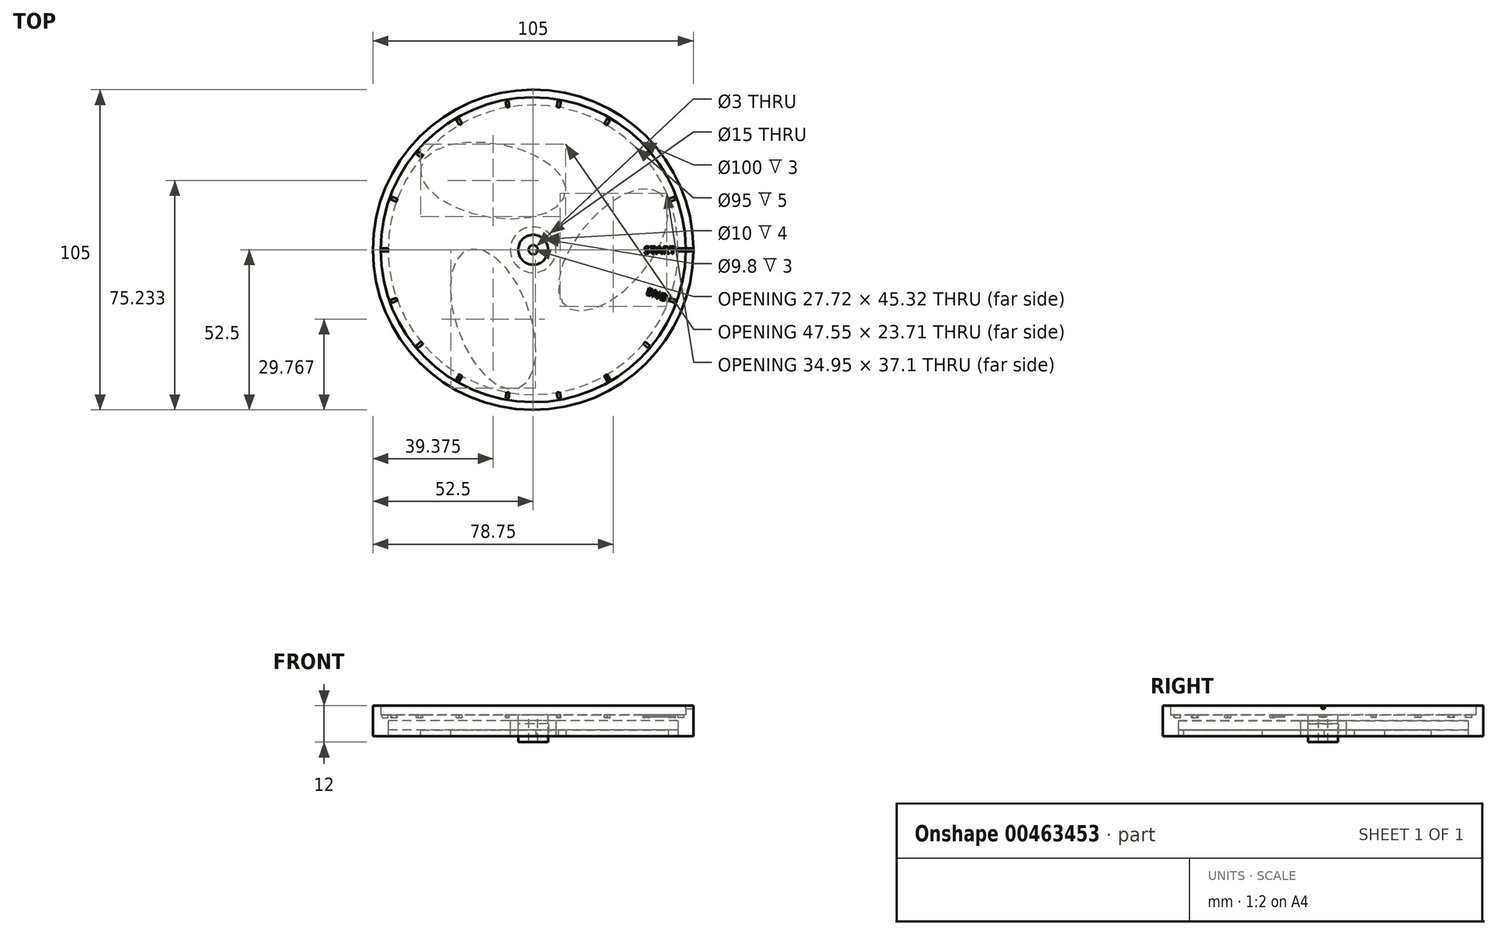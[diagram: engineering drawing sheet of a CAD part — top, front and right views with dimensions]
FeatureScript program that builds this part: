
annotation { "Feature Type Name" : "Feature", "Feature Type Description" : "" }
export const myFeature = defineFeature(function(context is Context, id is Id, definition is map)
    precondition{}
    {
        {
            var Q0;
            Q0=qCreatedBy(makeId("Top.planeOp"),FACE);
            var sketch = newSketch(context, id + "F0", { "sketchPlane" : qUnion([Q0])});
            skCircle(sketch, "E0", {"center": v(0, 0) * mm, "radius": 50 * mm});
            skCircle(sketch, "E1", {"center": v(0, 0) * mm, "radius": 52.5 * mm});
            skPoint(sketch, "E2.middle", {"position": v(52.5, 0) * mm});
            skCircle(sketch, "E3", {"center": v(0, 0) * mm, "radius": 5 * mm});
            skCircle(sketch, "E4", {"center": v(0, 0) * mm, "radius": 7.5 * mm});
            skCircle(sketch, "E5", {"center": v(0, 0) * mm, "radius": 47.5 * mm});
            skEllipse(sketch, "E6", {"center": v(26.25, 0) * mm, "majorRadius": 24.13 * mm, "minorRadius": 12.04 * mm, "majorAxis": v(0.64, 0.77)});
            skFitSpline(sketch, "E7.0", {"points": [v(47.3, 21.48) * mm, v(45.63, 23.18) * mm, v(43.65, 24.52) * mm, v(41.5, 25.44) * mm, v(39.28, 25.95) * mm, v(37.04, 26.11) * mm, v(34.8, 25.97) * mm, v(31.85, 25.42) * mm, v(28.25, 24.17) * mm, v(24.72, 22.3) * mm, v(21.93, 20.46) * mm, v(19.22, 18.43) * mm, v(16.62, 16.12) * mm, v(14.16, 13.59) * mm, v(12.4, 11.58) * mm, v(10.73, 9.49) * mm, v(8.67, 6.62) * mm, v(6.87, 3.65) * mm, v(5.35, 0.62) * mm, v(4.03, -2.45) * mm, v(2.81, -6.26) * mm, v(2.23, -10.02) * mm, v(2.21, -13.03) * mm, v(2.47, -15.25) * mm, v(3.02, -17.43) * mm, v(3.92, -19.53) * mm, v(5.2, -21.48) * mm, v(6.87, -23.18) * mm, v(8.85, -24.52) * mm, v(11, -25.44) * mm, v(13.22, -25.95) * mm, v(15.46, -26.11) * mm, v(17.7, -25.97) * mm, v(20.65, -25.42) * mm, v(24.25, -24.17) * mm, v(27.78, -22.3) * mm, v(30.57, -20.46) * mm, v(33.28, -18.43) * mm, v(35.88, -16.12) * mm, v(38.34, -13.59) * mm, v(40.1, -11.58) * mm, v(41.77, -9.49) * mm, v(43.83, -6.62) * mm, v(45.63, -3.65) * mm, v(47.15, -0.62) * mm, v(48.47, 2.45) * mm, v(49.69, 6.26) * mm, v(50.27, 10.02) * mm, v(50.29, 13.03) * mm, v(50.03, 15.25) * mm, v(49.48, 17.43) * mm, v(48.58, 19.53) * mm, v(47.3, 21.48) * mm, v(45.63, 23.18) * mm, v(43.65, 24.52) * mm, v(47.3, 21.48) * mm]});
            skEllipse(sketch, "E8.1.0", {"center": v(-13.12, 22.73) * mm, "majorRadius": 24.13 * mm, "minorRadius": 12.04 * mm, "majorAxis": v(-0.99, 0.17)});
            skEllipse(sketch, "E8.2.0", {"center": v(-13.13, -22.73) * mm, "majorRadius": 24.13 * mm, "minorRadius": 12.04 * mm, "majorAxis": v(0.34, -0.94)});
            skFitSpline(sketch, "E9.0", {"points": [v(-42.25, 30.22) * mm, v(-42.89, 27.92) * mm, v(-43.06, 25.54) * mm, v(-42.78, 23.23) * mm, v(-42.11, 21.04) * mm, v(-41.13, 19.02) * mm, v(-39.9, 17.16) * mm, v(-37.94, 14.87) * mm, v(-35.06, 12.37) * mm, v(-31.67, 10.25) * mm, v(-28.69, 8.76) * mm, v(-25.57, 7.43) * mm, v(-22.27, 6.33) * mm, v(-18.85, 5.47) * mm, v(-16.23, 4.94) * mm, v(-13.58, 4.55) * mm, v(-10.07, 4.2) * mm, v(-6.6, 4.12) * mm, v(-3.2, 4.32) * mm, v(0.1, 4.71) * mm, v(4.01, 5.56) * mm, v(7.57, 6.94) * mm, v(10.18, 8.43) * mm, v(11.97, 9.76) * mm, v(13.58, 11.33) * mm, v(14.95, 13.16) * mm, v(16, 15.25) * mm, v(16.64, 17.54) * mm, v(16.81, 19.92) * mm, v(16.53, 22.24) * mm, v(15.86, 24.43) * mm, v(14.88, 26.45) * mm, v(13.64, 28.3) * mm, v(11.7, 30.6) * mm, v(8.8, 33.1) * mm, v(5.42, 35.21) * mm, v(2.44, 36.7) * mm, v(-0.68, 38.04) * mm, v(-3.98, 39.14) * mm, v(-7.4, 40) * mm, v(-10.02, 40.52) * mm, v(-12.67, 40.92) * mm, v(-16.18, 41.26) * mm, v(-19.65, 41.34) * mm, v(-23.04, 41.15) * mm, v(-26.36, 40.75) * mm, v(-30.26, 39.9) * mm, v(-33.82, 38.53) * mm, v(-36.43, 37.04) * mm, v(-38.22, 35.7) * mm, v(-39.83, 34.13) * mm, v(-41.2, 32.3) * mm, v(-42.25, 30.22) * mm, v(-42.89, 27.92) * mm, v(-43.06, 25.54) * mm, v(-42.25, 30.22) * mm]});
            skFitSpline(sketch, "E10.0", {"points": [v(-5.04, -51.7) * mm, v(-2.74, -51.1) * mm, v(-0.6, -50.06) * mm, v(1.28, -48.66) * mm, v(2.84, -47) * mm, v(4.1, -45.13) * mm, v(5.09, -43.13) * mm, v(6.1, -40.3) * mm, v(6.81, -36.55) * mm, v(6.96, -32.56) * mm, v(6.75, -29.22) * mm, v(6.35, -25.85) * mm, v(5.65, -22.45) * mm, v(4.69, -19.06) * mm, v(3.83, -16.52) * mm, v(2.85, -14.04) * mm, v(1.4, -10.82) * mm, v(-0.27, -7.77) * mm, v(-2.14, -4.94) * mm, v(-4.14, -2.26) * mm, v(-6.82, 0.7) * mm, v(-9.8, 3.08) * mm, v(-12.39, 4.6) * mm, v(-14.44, 5.49) * mm, v(-16.6, 6.1) * mm, v(-18.87, 6.37) * mm, v(-21.2, 6.23) * mm, v(-23.51, 5.64) * mm, v(-25.66, 4.6) * mm, v(-27.53, 3.2) * mm, v(-29.09, 1.53) * mm, v(-30.35, -0.33) * mm, v(-31.34, -2.34) * mm, v(-32.34, -5.17) * mm, v(-33.06, -8.92) * mm, v(-33.2, -12.9) * mm, v(-33, -16.24) * mm, v(-32.6, -19.61) * mm, v(-31.9, -23.02) * mm, v(-30.94, -26.4) * mm, v(-30.08, -28.94) * mm, v(-29.1, -31.43) * mm, v(-27.65, -34.64) * mm, v(-25.98, -37.7) * mm, v(-24.11, -40.53) * mm, v(-22.11, -43.2) * mm, v(-19.43, -46.16) * mm, v(-16.46, -48.55) * mm, v(-13.86, -50.06) * mm, v(-11.8, -50.96) * mm, v(-9.65, -51.56) * mm, v(-7.38, -51.83) * mm, v(-5.04, -51.7) * mm, v(-2.74, -51.1) * mm, v(-0.6, -50.06) * mm, v(-5.04, -51.7) * mm]});
            skSolve(sketch);
        }
        {
            var Q0;
            {var subQ0=sQuery(id+"F0.wireOp",EDGE,"E9.0");var subQ1=sQuery(id+"F0.wireOp",EDGE,"E0");var subQ2=makeQuery(id+"F0.imprint","INTERSECT",VERTEX,{"disambiguationData":[OD(1.0)],"derivedFrom":[subQ1,subQ0]});Q0=makeQuery(id+"F0.imprint","IMPRINT",FACE,{"disambiguationData":[TD([[makeQuery(id+"F0.imprint","IMPRINT",EDGE,{"disambiguationData":[TD([[subQ2,-1.0]])],"derivedFrom":subQ1}),1.0]])]});}
            var Q1;
            {var subQ0=sQuery(id+"F0.wireOp",EDGE,"E10.0");var subQ1=sQuery(id+"F0.wireOp",EDGE,"E0");var subQ2=makeQuery(id+"F0.imprint","INTERSECT",VERTEX,{"disambiguationData":[OD(0.0)],"derivedFrom":[subQ1,subQ0]});Q1=makeQuery(id+"F0.imprint","IMPRINT",FACE,{"disambiguationData":[TD([[makeQuery(id+"F0.imprint","IMPRINT",EDGE,{"disambiguationData":[TD([[subQ2,-1.0]])],"derivedFrom":subQ1}),1.0]])]});}
            var Q2;
            {var subQ0=sQuery(id+"F0.wireOp",EDGE,"E7.0");var subQ1=sQuery(id+"F0.wireOp",EDGE,"E0");var subQ2=makeQuery(id+"F0.imprint","INTERSECT",VERTEX,{"disambiguationData":[OD(1.0)],"derivedFrom":[subQ1,subQ0]});Q2=makeQuery(id+"F0.imprint","IMPRINT",FACE,{"disambiguationData":[TD([[makeQuery(id+"F0.imprint","IMPRINT",EDGE,{"disambiguationData":[TD([[subQ2,1.0]])],"derivedFrom":subQ1}),1.0]])]});}
            var Q3;
            {var subQ0=sQuery(id+"F0.wireOp",EDGE,"E7.0");var subQ1=sQuery(id+"F0.wireOp",EDGE,"E0");var subQ2=makeQuery(id+"F0.imprint","INTERSECT",VERTEX,{"disambiguationData":[OD(0.0)],"derivedFrom":[subQ1,subQ0]});Q3=makeQuery(id+"F0.imprint","IMPRINT",FACE,{"disambiguationData":[TD([[makeQuery(id+"F0.imprint","IMPRINT",EDGE,{"disambiguationData":[TD([[subQ2,1.0]])],"derivedFrom":subQ1}),1.0]])]});}
            var Q4;
            {var subQ0=sQuery(id+"F0.wireOp",EDGE,"E7.0");var subQ1=sQuery(id+"F0.wireOp",EDGE,"E0");var subQ2=makeQuery(id+"F0.imprint","INTERSECT",VERTEX,{"disambiguationData":[OD(0.0)],"derivedFrom":[subQ1,subQ0]});Q4=makeQuery(id+"F0.imprint","IMPRINT",FACE,{"disambiguationData":[TD([[makeQuery(id+"F0.imprint","IMPRINT",EDGE,{"disambiguationData":[TD([[subQ2,-1.0]])],"derivedFrom":subQ1}),1.0]])]});}
            var Q5;
            {var subQ0=sQuery(id+"F0.wireOp",EDGE,"E9.0");var subQ1=sQuery(id+"F0.wireOp",EDGE,"E0");var subQ2=makeQuery(id+"F0.imprint","INTERSECT",VERTEX,{"disambiguationData":[OD(0.0)],"derivedFrom":[subQ1,subQ0]});Q5=makeQuery(id+"F0.imprint","IMPRINT",FACE,{"disambiguationData":[TD([[makeQuery(id+"F0.imprint","IMPRINT",EDGE,{"disambiguationData":[TD([[subQ2,-1.0]])],"derivedFrom":subQ1}),1.0]])]});}
            var Q6;
            Q6=makeQuery(id+"F0.imprint","IMPRINT",FACE,{"disambiguationData":[TD([[makeQuery(id+"F0.imprint","IMPRINT",EDGE,{"derivedFrom":sQuery(id+"F0.wireOp",EDGE,"5SP7GSyY-g8OX-zm8A-jqP5-KDN9Loz0VI4X")}),-1.0]])]});
            var Q7;
            {var subQ0=sQuery(id+"F0.wireOp",EDGE,"E9.0");var subQ1=sQuery(id+"F0.wireOp",EDGE,"E3");var subQ2=makeQuery(id+"F0.imprint","INTERSECT",VERTEX,{"disambiguationData":[OD(0.0)],"derivedFrom":[subQ1,subQ0]});Q7=makeQuery(id+"F0.imprint","IMPRINT",FACE,{"disambiguationData":[TD([[makeQuery(id+"F0.imprint","IMPRINT",EDGE,{"disambiguationData":[TD([[subQ2,-1.0]])],"derivedFrom":subQ1}),-1.0]])]});}
            var Q8;
            {var subQ0=sQuery(id+"F0.wireOp",EDGE,"E9.0");var subQ1=sQuery(id+"F0.wireOp",EDGE,"E3");var subQ2=makeQuery(id+"F0.imprint","INTERSECT",VERTEX,{"disambiguationData":[OD(0.0)],"derivedFrom":[subQ1,subQ0]});Q8=makeQuery(id+"F0.imprint","IMPRINT",FACE,{"disambiguationData":[TD([[makeQuery(id+"F0.imprint","IMPRINT",EDGE,{"disambiguationData":[TD([[subQ2,1.0]])],"derivedFrom":subQ1}),-1.0]])]});}
            var Q9;
            {var subQ0=sQuery(id+"F0.wireOp",EDGE,"E9.0");var subQ1=sQuery(id+"F0.wireOp",EDGE,"E3");var subQ2=makeQuery(id+"F0.imprint","INTERSECT",VERTEX,{"disambiguationData":[OD(1.0)],"derivedFrom":[subQ1,subQ0]});Q9=makeQuery(id+"F0.imprint","IMPRINT",FACE,{"disambiguationData":[TD([[makeQuery(id+"F0.imprint","IMPRINT",EDGE,{"disambiguationData":[TD([[subQ2,1.0]])],"derivedFrom":subQ1}),-1.0]])]});}
            var Q10;
            {var subQ0=sQuery(id+"F0.wireOp",EDGE,"E7.0");var subQ1=sQuery(id+"F0.wireOp",EDGE,"E3");var subQ2=makeQuery(id+"F0.imprint","INTERSECT",VERTEX,{"disambiguationData":[OD(0.0)],"derivedFrom":[subQ1,subQ0]});Q10=makeQuery(id+"F0.imprint","IMPRINT",FACE,{"disambiguationData":[TD([[makeQuery(id+"F0.imprint","IMPRINT",EDGE,{"disambiguationData":[TD([[subQ2,-1.0]])],"derivedFrom":subQ1}),-1.0]])]});}
            var Q11;
            {var subQ0=sQuery(id+"F0.wireOp",EDGE,"E10.0");var subQ1=sQuery(id+"F0.wireOp",EDGE,"E3");var subQ2=makeQuery(id+"F0.imprint","INTERSECT",VERTEX,{"disambiguationData":[OD(0.0)],"derivedFrom":[subQ1,subQ0]});Q11=makeQuery(id+"F0.imprint","IMPRINT",FACE,{"disambiguationData":[TD([[makeQuery(id+"F0.imprint","IMPRINT",EDGE,{"disambiguationData":[TD([[subQ2,-1.0]])],"derivedFrom":subQ1}),-1.0]])]});}
            var Q12;
            {var subQ0=sQuery(id+"F0.wireOp",EDGE,"E10.0");var subQ1=sQuery(id+"F0.wireOp",EDGE,"E3");var subQ2=makeQuery(id+"F0.imprint","INTERSECT",VERTEX,{"disambiguationData":[OD(1.0)],"derivedFrom":[subQ1,subQ0]});Q12=makeQuery(id+"F0.imprint","IMPRINT",FACE,{"disambiguationData":[TD([[makeQuery(id+"F0.imprint","IMPRINT",EDGE,{"disambiguationData":[TD([[subQ2,-1.0]])],"derivedFrom":subQ1}),-1.0]])]});}
            extrude(context, id + "F1", {"entities" : qUnion([Q0, Q1, Q2, Q3, Q4, Q5, Q6, Q7, Q8, Q9, Q10, Q11, Q12]), "depth" : 7 * mm});
        }
        {
            var Q0;
            Q0=makeQuery(id+"F0.imprint","IMPRINT",FACE,{"disambiguationData":[TD([[makeQuery(id+"F0.imprint","IMPRINT",EDGE,{"derivedFrom":sQuery(id+"F0.wireOp",EDGE,"E1")}),1.0]])]});
            var Q1;
            {var subQ0=sQuery(id+"F0.wireOp",EDGE,"E7.0");var subQ1=sQuery(id+"F0.wireOp",EDGE,"E0");var subQ2=makeQuery(id+"F0.imprint","INTERSECT",VERTEX,{"disambiguationData":[OD(0.0)],"derivedFrom":[subQ1,subQ0]});Q1=makeQuery(id+"F0.imprint","IMPRINT",FACE,{"disambiguationData":[TD([[makeQuery(id+"F0.imprint","IMPRINT",EDGE,{"disambiguationData":[TD([[subQ2,1.0]])],"derivedFrom":subQ1}),-1.0]])]});}
            var Q2;
            {var subQ0=sQuery(id+"F0.wireOp",EDGE,"E10.0");var subQ1=sQuery(id+"F0.wireOp",EDGE,"E0");var subQ2=makeQuery(id+"F0.imprint","INTERSECT",VERTEX,{"disambiguationData":[OD(0.0)],"derivedFrom":[subQ1,subQ0]});Q2=makeQuery(id+"F0.imprint","IMPRINT",FACE,{"disambiguationData":[TD([[makeQuery(id+"F0.imprint","IMPRINT",EDGE,{"disambiguationData":[TD([[subQ2,-1.0]])],"derivedFrom":subQ1}),-1.0]])]});}
            var Q3;
            {var subQ0=sQuery(id+"F0.wireOp",EDGE,"E9.0");var subQ1=sQuery(id+"F0.wireOp",EDGE,"E0");var subQ2=makeQuery(id+"F0.imprint","INTERSECT",VERTEX,{"disambiguationData":[OD(0.0)],"derivedFrom":[subQ1,subQ0]});Q3=makeQuery(id+"F0.imprint","IMPRINT",FACE,{"disambiguationData":[TD([[makeQuery(id+"F0.imprint","IMPRINT",EDGE,{"disambiguationData":[TD([[subQ2,-1.0]])],"derivedFrom":subQ1}),-1.0]])]});}
            extrude(context, id + "F2", {"entities" : qUnion([Q0, Q1, Q2, Q3]), "operationType" : NewBodyOperationType.ADD, "depth" : 10 * mm});
        }
        {
            var Q0;
            Q0=makeQuery(id+"F0.imprint","IMPRINT",FACE,{"disambiguationData":[TD([[makeQuery(id+"F0.imprint","IMPRINT",EDGE,{"derivedFrom":sQuery(id+"F0.wireOp",EDGE,"E8.1.0")}),-1.0]])]});
            var Q1;
            {var subQ0=sQuery(id+"F0.wireOp",EDGE,"E10.0");var subQ1=sQuery(id+"F0.wireOp",EDGE,"E9.0");var subQ2=makeQuery(id+"F0.imprint","INTERSECT",VERTEX,{"disambiguationData":[OD(0.0)],"derivedFrom":[subQ1,subQ0]});Q1=makeQuery(id+"F0.imprint","IMPRINT",FACE,{"disambiguationData":[TD([[makeQuery(id+"F0.imprint","IMPRINT",EDGE,{"disambiguationData":[TD([[subQ2,-1.0]])],"derivedFrom":subQ1}),1.0]])]});}
            var Q2;
            Q2=makeQuery(id+"F0.imprint","IMPRINT",FACE,{"disambiguationData":[TD([[makeQuery(id+"F0.imprint","IMPRINT",EDGE,{"derivedFrom":sQuery(id+"F0.wireOp",EDGE,"E8.2.0")}),-1.0]])]});
            var Q3;
            {var subQ0=sQuery(id+"F0.wireOp",EDGE,"E9.0");var subQ1=sQuery(id+"F0.wireOp",EDGE,"E4");var subQ2=makeQuery(id+"F0.imprint","INTERSECT",VERTEX,{"disambiguationData":[OD(1.0)],"derivedFrom":[subQ1,subQ0]});Q3=makeQuery(id+"F0.imprint","IMPRINT",FACE,{"disambiguationData":[TD([[makeQuery(id+"F0.imprint","IMPRINT",EDGE,{"disambiguationData":[TD([[subQ2,-1.0]])],"derivedFrom":subQ1}),-1.0]])]});}
            var Q4;
            {var subQ0=sQuery(id+"F0.wireOp",EDGE,"E10.0");var subQ1=sQuery(id+"F0.wireOp",EDGE,"E4");var subQ2=makeQuery(id+"F0.imprint","INTERSECT",VERTEX,{"disambiguationData":[OD(1.0)],"derivedFrom":[subQ1,subQ0]});Q4=makeQuery(id+"F0.imprint","IMPRINT",FACE,{"disambiguationData":[TD([[makeQuery(id+"F0.imprint","IMPRINT",EDGE,{"disambiguationData":[TD([[subQ2,-1.0]])],"derivedFrom":subQ1}),-1.0]])]});}
            var Q5;
            {var subQ0=sQuery(id+"F0.wireOp",EDGE,"E10.0");var subQ1=sQuery(id+"F0.wireOp",EDGE,"E7.0");var subQ2=makeQuery(id+"F0.imprint","INTERSECT",VERTEX,{"disambiguationData":[OD(0.0)],"derivedFrom":[subQ1,subQ0]});Q5=makeQuery(id+"F0.imprint","IMPRINT",FACE,{"disambiguationData":[TD([[makeQuery(id+"F0.imprint","IMPRINT",EDGE,{"disambiguationData":[TD([[subQ2,-1.0]])],"derivedFrom":subQ1}),1.0]])]});}
            var Q6;
            Q6=makeQuery(id+"F0.imprint","IMPRINT",FACE,{"disambiguationData":[TD([[makeQuery(id+"F0.imprint","IMPRINT",EDGE,{"derivedFrom":sQuery(id+"F0.wireOp",EDGE,"E6")}),-1.0]])]});
            var Q7;
            {var subQ0=sQuery(id+"F0.wireOp",EDGE,"E9.0");var subQ1=sQuery(id+"F0.wireOp",EDGE,"E4");var subQ2=makeQuery(id+"F0.imprint","INTERSECT",VERTEX,{"disambiguationData":[OD(0.0)],"derivedFrom":[subQ1,subQ0]});Q7=makeQuery(id+"F0.imprint","IMPRINT",FACE,{"disambiguationData":[TD([[makeQuery(id+"F0.imprint","IMPRINT",EDGE,{"disambiguationData":[TD([[subQ2,1.0]])],"derivedFrom":subQ1}),-1.0]])]});}
            var Q8;
            {var subQ0=sQuery(id+"F0.wireOp",EDGE,"E9.0");var subQ1=sQuery(id+"F0.wireOp",EDGE,"E7.0");var subQ2=makeQuery(id+"F0.imprint","INTERSECT",VERTEX,{"disambiguationData":[OD(0.0)],"derivedFrom":[subQ1,subQ0]});Q8=makeQuery(id+"F0.imprint","IMPRINT",FACE,{"disambiguationData":[TD([[makeQuery(id+"F0.imprint","IMPRINT",EDGE,{"disambiguationData":[TD([[subQ2,-1.0]])],"derivedFrom":subQ1}),1.0]])]});}
            extrude(context, id + "F3", {"entities" : qUnion([Q0, Q1, Q2, Q3, Q4, Q5, Q6, Q7, Q8]), "depth" : 2 * mm});
        }
        {
            var Q0;
            Q0=makeQuery(id+"F1.opExtrude","CAP_FACE",FACE,{"disambiguationData":[OSD([sQuery(id+"F0.wireOp",EDGE,"E3"),sQuery(id+"F0.wireOp",EDGE,"E4")])],"isStart":false});
            var sketch = newSketch(context, id + "F4", { "sketchPlane" : qUnion([Q0])});
            skCircle(sketch, "E11", {"center": v(0, 0) * mm, "radius": 4.9 * mm});
            skCircle(sketch, "E12", {"center": v(0, 0) * mm, "radius": 49.5 * mm});
            skCircle(sketch, "E13.0", {"center": v(0, 0) * mm, "radius": 47.5 * mm});
            skCircle(sketch, "E14", {"center": v(0, 0) * mm, "radius": 7.5 * mm});
            skSolve(sketch);
        }
        {
            var Q0;
            Q0=makeQuery(id+"F4.imprint","IMPRINT",FACE,{"disambiguationData":[TD([[makeQuery(id+"F4.imprint","IMPRINT",EDGE,{"derivedFrom":sQuery(id+"F4.wireOp",EDGE,"E11")}),1.0]])]});
            extrude(context, id + "F5", {"entities" : qUnion([Q0]), "oppositeDirection" : true, "depth" : 9 * mm});
        }
        {
            var Q0;
            Q0=makeQuery(id+"F4.imprint","IMPRINT",FACE,{"disambiguationData":[TD([[makeQuery(id+"F4.imprint","IMPRINT",EDGE,{"derivedFrom":sQuery(id+"F4.wireOp",EDGE,"E14")}),1.0]])]});
            var Q1;
            Q1=makeQuery(id+"F4.imprint","IMPRINT",FACE,{"disambiguationData":[TD([[makeQuery(id+"F4.imprint","IMPRINT",EDGE,{"derivedFrom":sQuery(id+"F4.wireOp",EDGE,"E11")}),-1.0]])]});
            extrude(context, id + "F6", {"entities" : qUnion([Q0, Q1]), "oppositeDirection" : true, "depth" : 3 * mm});
        }
        {
            var Q0;
            Q0=makeQuery(id+"F4.imprint","IMPRINT",FACE,{"disambiguationData":[TD([[makeQuery(id+"F4.imprint","IMPRINT",EDGE,{"derivedFrom":sQuery(id+"F4.wireOp",EDGE,"E13.0")}),1.0]])]});
            extrude(context, id + "F7", {"entities" : qUnion([Q0]), "operationType" : NewBodyOperationType.ADD, "oppositeDirection" : true, "depth" : 2 * mm});
        }
        {
            var Q0;
            Q0=makeQuery(id+"F4.imprint","IMPRINT",FACE,{"disambiguationData":[TD([[makeQuery(id+"F4.imprint","IMPRINT",EDGE,{"derivedFrom":sQuery(id+"F4.wireOp",EDGE,"E12")}),1.0]])]});
            extrude(context, id + "F8", {"entities" : qUnion([Q0]), "operationType" : NewBodyOperationType.ADD, "oppositeDirection" : true, "depth" : 3 * mm});
        }
        {
            var Q0;
            Q0=makeQuery(id+"F2.opExtrude","CAP_FACE",FACE,{"disambiguationData":[OSD([sQuery(id+"F0.wireOp",EDGE,"E0"),sQuery(id+"F0.wireOp",EDGE,"E1")])],"isStart":false});
            var sketch = newSketch(context, id + "F9", { "sketchPlane" : qUnion([Q0])});
            skLineSegment(sketch, "E15", {"start": v(0, 0) * mm, "end": v(52.5, 0) * mm, "construction": true});
            skLineSegment(sketch, "E16.bottom", {"start": v(49.7, -0.5) * mm, "end": v(55.3, -0.5) * mm});
            skLineSegment(sketch, "E16.top", {"start": v(49.7, 0.5) * mm, "end": v(55.3, 0.5) * mm});
            skLineSegment(sketch, "E16.left", {"start": v(49.7, -0.5) * mm, "end": v(49.7, 0.5) * mm});
            skLineSegment(sketch, "E16.right", {"start": v(55.3, -0.5) * mm, "end": v(55.3, 0.5) * mm});
            skPoint(sketch, "E16.middle", {"position": v(52.5, 0) * mm});
            skSolve(sketch);
        }
        {
            var Q0;
            {var subQ0=sQuery(id+"F9.wireOp",EDGE,"E16.bottom");var subQ1=makeQuery(id+"F2.opExtrude","CAP_EDGE",EDGE,{"disambiguationData":[OSD([sQuery(id+"F0.wireOp",EDGE,"E1")])],"isStart":false});var subQ2=makeQuery(id+"F9.imprint","INTERSECT",VERTEX,{"derivedFrom":[subQ1,subQ0]});Q0=makeQuery(id+"F9.imprint","IMPRINT",FACE,{"disambiguationData":[TD([[makeQuery(id+"F9.imprint","IMPRINT",EDGE,{"disambiguationData":[TD([[subQ2,1.0]])],"derivedFrom":subQ0}),1.0]])]});}
            extrude(context, id + "F10", {"entities" : qUnion([Q0]), "operationType" : NewBodyOperationType.REMOVE, "oppositeDirection" : true, "depth" : 1 * mm});
        }
        {
            var Q0;
            Q0=makeQuery(id+"F4.imprint","IMPRINT",FACE,{"disambiguationData":[TD([[makeQuery(id+"F4.imprint","IMPRINT",EDGE,{"derivedFrom":sQuery(id+"F4.wireOp",EDGE,"E12")}),1.0]])]});
            var sketch = newSketch(context, id + "F11", { "sketchPlane" : qUnion([Q0])});
            skCircle(sketch, "E17.0", {"center": v(0, 0) * mm, "radius": 47.5 * mm});
            skCircle(sketch, "E18.0", {"center": v(0, 0) * mm, "radius": 49.5 * mm});
            skLineSegment(sketch, "E19", {"start": v(0, 0) * mm, "end": v(49.5, 0) * mm, "construction": true});
            skLineSegment(sketch, "E20.bottom", {"start": v(52.3, -0.5) * mm, "end": v(46.7, -0.5) * mm});
            skLineSegment(sketch, "E20.top", {"start": v(52.3, 0.5) * mm, "end": v(46.7, 0.5) * mm});
            skLineSegment(sketch, "E20.left", {"start": v(52.3, -0.5) * mm, "end": v(52.3, 0.5) * mm});
            skLineSegment(sketch, "E20.right", {"start": v(46.7, -0.5) * mm, "end": v(46.7, 0.5) * mm});
            skPoint(sketch, "E20.middle", {"position": v(49.5, 0) * mm});
            skLineSegment(sketch, "E21.1.0", {"start": v(49.31, -17.42) * mm, "end": v(44.06, -15.5) * mm});
            skLineSegment(sketch, "E21.1.1", {"start": v(48.97, -18.36) * mm, "end": v(43.72, -16.44) * mm});
            skLineSegment(sketch, "E21.1.2", {"start": v(43.72, -16.44) * mm, "end": v(44.06, -15.5) * mm});
            skLineSegment(sketch, "E21.1.3", {"start": v(48.97, -18.36) * mm, "end": v(49.31, -17.42) * mm});
            skLineSegment(sketch, "E21.2.0", {"start": v(40.38, -33.23) * mm, "end": v(36.1, -29.64) * mm});
            skLineSegment(sketch, "E21.2.1", {"start": v(39.74, -34) * mm, "end": v(35.46, -30.4) * mm});
            skLineSegment(sketch, "E21.2.2", {"start": v(35.46, -30.4) * mm, "end": v(36.1, -29.64) * mm});
            skLineSegment(sketch, "E21.2.3", {"start": v(39.74, -34) * mm, "end": v(40.38, -33.23) * mm});
            skLineSegment(sketch, "E21.3.0", {"start": v(26.58, -45.04) * mm, "end": v(23.79, -40.2) * mm});
            skLineSegment(sketch, "E21.3.1", {"start": v(25.71, -45.54) * mm, "end": v(22.92, -40.7) * mm});
            skLineSegment(sketch, "E21.3.2", {"start": v(22.92, -40.7) * mm, "end": v(23.79, -40.2) * mm});
            skLineSegment(sketch, "E21.3.3", {"start": v(25.71, -45.54) * mm, "end": v(26.58, -45.04) * mm});
            skLineSegment(sketch, "E21.4.0", {"start": v(9.57, -51.41) * mm, "end": v(8.6, -45.91) * mm});
            skLineSegment(sketch, "E21.4.1", {"start": v(8.59, -51.59) * mm, "end": v(7.62, -46.08) * mm});
            skLineSegment(sketch, "E21.4.2", {"start": v(7.62, -46.08) * mm, "end": v(8.6, -45.91) * mm});
            skLineSegment(sketch, "E21.4.3", {"start": v(8.59, -51.59) * mm, "end": v(9.57, -51.41) * mm});
            skLineSegment(sketch, "E21.5.0", {"start": v(-8.59, -51.59) * mm, "end": v(-7.62, -46.08) * mm});
            skLineSegment(sketch, "E21.5.1", {"start": v(-9.57, -51.41) * mm, "end": v(-8.6, -45.91) * mm});
            skLineSegment(sketch, "E21.5.2", {"start": v(-8.6, -45.91) * mm, "end": v(-7.62, -46.08) * mm});
            skLineSegment(sketch, "E21.5.3", {"start": v(-9.57, -51.41) * mm, "end": v(-8.59, -51.59) * mm});
            skLineSegment(sketch, "E21.6.0", {"start": v(-25.71, -45.54) * mm, "end": v(-22.92, -40.7) * mm});
            skLineSegment(sketch, "E21.6.1", {"start": v(-26.58, -45.04) * mm, "end": v(-23.79, -40.2) * mm});
            skLineSegment(sketch, "E21.6.2", {"start": v(-23.79, -40.2) * mm, "end": v(-22.92, -40.7) * mm});
            skLineSegment(sketch, "E21.6.3", {"start": v(-26.58, -45.04) * mm, "end": v(-25.71, -45.54) * mm});
            skLineSegment(sketch, "E21.7.0", {"start": v(-39.74, -34) * mm, "end": v(-35.46, -30.4) * mm});
            skLineSegment(sketch, "E21.7.1", {"start": v(-40.38, -33.23) * mm, "end": v(-36.1, -29.64) * mm});
            skLineSegment(sketch, "E21.7.2", {"start": v(-36.1, -29.64) * mm, "end": v(-35.46, -30.4) * mm});
            skLineSegment(sketch, "E21.7.3", {"start": v(-40.38, -33.23) * mm, "end": v(-39.74, -34) * mm});
            skLineSegment(sketch, "E21.8.0", {"start": v(-48.97, -18.36) * mm, "end": v(-43.72, -16.44) * mm});
            skLineSegment(sketch, "E21.8.1", {"start": v(-49.31, -17.42) * mm, "end": v(-44.06, -15.5) * mm});
            skLineSegment(sketch, "E21.8.2", {"start": v(-44.06, -15.5) * mm, "end": v(-43.72, -16.44) * mm});
            skLineSegment(sketch, "E21.8.3", {"start": v(-49.31, -17.42) * mm, "end": v(-48.97, -18.36) * mm});
            skLineSegment(sketch, "E21.9.0", {"start": v(-52.3, -0.5) * mm, "end": v(-46.7, -0.5) * mm});
            skLineSegment(sketch, "E21.9.1", {"start": v(-52.3, 0.5) * mm, "end": v(-46.7, 0.5) * mm});
            skLineSegment(sketch, "E21.9.2", {"start": v(-46.7, 0.5) * mm, "end": v(-46.7, -0.5) * mm});
            skLineSegment(sketch, "E21.9.3", {"start": v(-52.3, 0.5) * mm, "end": v(-52.3, -0.5) * mm});
            skLineSegment(sketch, "E21.10.0", {"start": v(-49.31, 17.42) * mm, "end": v(-44.06, 15.5) * mm});
            skLineSegment(sketch, "E21.10.1", {"start": v(-48.97, 18.36) * mm, "end": v(-43.72, 16.44) * mm});
            skLineSegment(sketch, "E21.10.2", {"start": v(-43.72, 16.44) * mm, "end": v(-44.06, 15.5) * mm});
            skLineSegment(sketch, "E21.10.3", {"start": v(-48.97, 18.36) * mm, "end": v(-49.31, 17.42) * mm});
            skLineSegment(sketch, "E21.11.0", {"start": v(-40.38, 33.23) * mm, "end": v(-36.1, 29.64) * mm});
            skLineSegment(sketch, "E21.11.1", {"start": v(-39.74, 34) * mm, "end": v(-35.46, 30.4) * mm});
            skLineSegment(sketch, "E21.11.2", {"start": v(-35.46, 30.4) * mm, "end": v(-36.1, 29.64) * mm});
            skLineSegment(sketch, "E21.11.3", {"start": v(-39.74, 34) * mm, "end": v(-40.38, 33.23) * mm});
            skLineSegment(sketch, "E21.12.0", {"start": v(-26.58, 45.04) * mm, "end": v(-23.79, 40.2) * mm});
            skLineSegment(sketch, "E21.12.1", {"start": v(-25.71, 45.54) * mm, "end": v(-22.92, 40.7) * mm});
            skLineSegment(sketch, "E21.12.2", {"start": v(-22.92, 40.7) * mm, "end": v(-23.79, 40.2) * mm});
            skLineSegment(sketch, "E21.12.3", {"start": v(-25.71, 45.54) * mm, "end": v(-26.58, 45.04) * mm});
            skLineSegment(sketch, "E21.13.0", {"start": v(-9.57, 51.41) * mm, "end": v(-8.6, 45.91) * mm});
            skLineSegment(sketch, "E21.13.1", {"start": v(-8.59, 51.59) * mm, "end": v(-7.62, 46.08) * mm});
            skLineSegment(sketch, "E21.13.2", {"start": v(-7.62, 46.08) * mm, "end": v(-8.6, 45.91) * mm});
            skLineSegment(sketch, "E21.13.3", {"start": v(-8.59, 51.59) * mm, "end": v(-9.57, 51.41) * mm});
            skLineSegment(sketch, "E21.14.0", {"start": v(8.59, 51.59) * mm, "end": v(7.62, 46.08) * mm});
            skLineSegment(sketch, "E21.14.1", {"start": v(9.57, 51.41) * mm, "end": v(8.6, 45.91) * mm});
            skLineSegment(sketch, "E21.14.2", {"start": v(8.6, 45.91) * mm, "end": v(7.62, 46.08) * mm});
            skLineSegment(sketch, "E21.14.3", {"start": v(9.57, 51.41) * mm, "end": v(8.59, 51.59) * mm});
            skLineSegment(sketch, "E21.15.0", {"start": v(25.71, 45.54) * mm, "end": v(22.92, 40.7) * mm});
            skLineSegment(sketch, "E21.15.1", {"start": v(26.58, 45.04) * mm, "end": v(23.79, 40.2) * mm});
            skLineSegment(sketch, "E21.15.2", {"start": v(23.79, 40.2) * mm, "end": v(22.92, 40.7) * mm});
            skLineSegment(sketch, "E21.15.3", {"start": v(26.58, 45.04) * mm, "end": v(25.71, 45.54) * mm});
            skLineSegment(sketch, "E21.16.0", {"start": v(39.74, 34) * mm, "end": v(35.46, 30.4) * mm});
            skLineSegment(sketch, "E21.16.1", {"start": v(40.38, 33.23) * mm, "end": v(36.1, 29.64) * mm});
            skLineSegment(sketch, "E21.16.2", {"start": v(36.1, 29.64) * mm, "end": v(35.46, 30.4) * mm});
            skLineSegment(sketch, "E21.16.3", {"start": v(40.38, 33.23) * mm, "end": v(39.74, 34) * mm});
            skLineSegment(sketch, "E21.17.0", {"start": v(48.97, 18.36) * mm, "end": v(43.72, 16.44) * mm});
            skLineSegment(sketch, "E21.17.1", {"start": v(49.31, 17.42) * mm, "end": v(44.06, 15.5) * mm});
            skLineSegment(sketch, "E21.17.2", {"start": v(44.06, 15.5) * mm, "end": v(43.72, 16.44) * mm});
            skLineSegment(sketch, "E21.17.3", {"start": v(49.31, 17.42) * mm, "end": v(48.97, 18.36) * mm});
            skLineSegment(sketch, "E21.anchor1", {"start": v(0, 0) * mm, "end": v(46.7, -0.5) * mm, "construction": true});
            skLineSegment(sketch, "E21.anchor2", {"start": v(0, 0) * mm, "end": v(44.06, 15.5) * mm, "construction": true});
            skLineSegment(sketch, "E22", {"start": v(0, 0) * mm, "end": v(36.1, 29.64) * mm, "construction": true});
            skLineSegment(sketch, "E23", {"start": v(0, 0) * mm, "end": v(43.72, -16.44) * mm, "construction": true});
            skLineSegment(sketch, "E24", {"start": v(0, 0) * mm, "end": v(35.46, -30.4) * mm, "construction": true});
            skLineSegment(sketch, "E25", {"start": v(22.92, -40.7) * mm, "end": v(0, 0) * mm, "construction": true});
            skLineSegment(sketch, "E26", {"start": v(0, 0) * mm, "end": v(7.62, -46.08) * mm, "construction": true});
            skLineSegment(sketch, "E27", {"start": v(-8.6, -45.91) * mm, "end": v(0, 0) * mm, "construction": true});
            skLineSegment(sketch, "E28", {"start": v(0, 0) * mm, "end": v(-23.79, -40.2) * mm, "construction": true});
            skLineSegment(sketch, "E29", {"start": v(-36.1, -29.64) * mm, "end": v(0, 0) * mm, "construction": true});
            skLineSegment(sketch, "E30", {"start": v(0, 0) * mm, "end": v(-44.06, -15.5) * mm, "construction": true});
            skLineSegment(sketch, "E31", {"start": v(-46.7, 0.5) * mm, "end": v(0, 0) * mm, "construction": true});
            skLineSegment(sketch, "E32", {"start": v(0, 0) * mm, "end": v(-43.72, 16.44) * mm, "construction": true});
            skLineSegment(sketch, "E33", {"start": v(-35.46, 30.4) * mm, "end": v(0, 0) * mm, "construction": true});
            skLineSegment(sketch, "E34", {"start": v(0, 0) * mm, "end": v(-22.92, 40.7) * mm, "construction": true});
            skLineSegment(sketch, "E35", {"start": v(-7.62, 46.08) * mm, "end": v(0, 0) * mm, "construction": true});
            skLineSegment(sketch, "E36", {"start": v(0, 0) * mm, "end": v(8.6, 45.91) * mm, "construction": true});
            skLineSegment(sketch, "E37", {"start": v(23.79, 40.2) * mm, "end": v(0, 0) * mm, "construction": true});
            skSolve(sketch);
        }
        {
            var Q0;
            {var subQ0=sQuery(id+"F11.wireOp",EDGE,"E20.bottom");var subQ1=sQuery(id+"F11.wireOp",EDGE,"E17.0");var subQ2=makeQuery(id+"F11.imprint","INTERSECT",VERTEX,{"derivedFrom":[subQ1,subQ0]});Q0=makeQuery(id+"F11.imprint","IMPRINT",FACE,{"disambiguationData":[TD([[makeQuery(id+"F11.imprint","IMPRINT",EDGE,{"disambiguationData":[TD([[subQ2,-1.0]])],"derivedFrom":subQ1}),-1.0]])]});}
            var Q1;
            {var subQ0=sQuery(id+"F11.wireOp",EDGE,"E21.1.1");var subQ1=sQuery(id+"F11.wireOp",EDGE,"E17.0");var subQ2=makeQuery(id+"F11.imprint","INTERSECT",VERTEX,{"derivedFrom":[subQ1,subQ0]});Q1=makeQuery(id+"F11.imprint","IMPRINT",FACE,{"disambiguationData":[TD([[makeQuery(id+"F11.imprint","IMPRINT",EDGE,{"disambiguationData":[TD([[subQ2,-1.0]])],"derivedFrom":subQ1}),-1.0]])]});}
            var Q2;
            {var subQ0=sQuery(id+"F11.wireOp",EDGE,"E21.2.1");var subQ1=sQuery(id+"F11.wireOp",EDGE,"E17.0");var subQ2=makeQuery(id+"F11.imprint","INTERSECT",VERTEX,{"derivedFrom":[subQ1,subQ0]});Q2=makeQuery(id+"F11.imprint","IMPRINT",FACE,{"disambiguationData":[TD([[makeQuery(id+"F11.imprint","IMPRINT",EDGE,{"disambiguationData":[TD([[subQ2,-1.0]])],"derivedFrom":subQ1}),-1.0]])]});}
            var Q3;
            {var subQ0=sQuery(id+"F11.wireOp",EDGE,"E21.3.1");var subQ1=sQuery(id+"F11.wireOp",EDGE,"E17.0");var subQ2=makeQuery(id+"F11.imprint","INTERSECT",VERTEX,{"derivedFrom":[subQ1,subQ0]});Q3=makeQuery(id+"F11.imprint","IMPRINT",FACE,{"disambiguationData":[TD([[makeQuery(id+"F11.imprint","IMPRINT",EDGE,{"disambiguationData":[TD([[subQ2,-1.0]])],"derivedFrom":subQ1}),-1.0]])]});}
            var Q4;
            {var subQ0=sQuery(id+"F11.wireOp",EDGE,"E21.4.1");var subQ1=sQuery(id+"F11.wireOp",EDGE,"E17.0");var subQ2=makeQuery(id+"F11.imprint","INTERSECT",VERTEX,{"derivedFrom":[subQ1,subQ0]});Q4=makeQuery(id+"F11.imprint","IMPRINT",FACE,{"disambiguationData":[TD([[makeQuery(id+"F11.imprint","IMPRINT",EDGE,{"disambiguationData":[TD([[subQ2,-1.0]])],"derivedFrom":subQ1}),-1.0]])]});}
            var Q5;
            {var subQ0=sQuery(id+"F11.wireOp",EDGE,"E21.5.1");var subQ1=sQuery(id+"F11.wireOp",EDGE,"E17.0");var subQ2=makeQuery(id+"F11.imprint","INTERSECT",VERTEX,{"derivedFrom":[subQ1,subQ0]});Q5=makeQuery(id+"F11.imprint","IMPRINT",FACE,{"disambiguationData":[TD([[makeQuery(id+"F11.imprint","IMPRINT",EDGE,{"disambiguationData":[TD([[subQ2,-1.0]])],"derivedFrom":subQ1}),-1.0]])]});}
            var Q6;
            {var subQ0=sQuery(id+"F11.wireOp",EDGE,"E21.6.1");var subQ1=sQuery(id+"F11.wireOp",EDGE,"E17.0");var subQ2=makeQuery(id+"F11.imprint","INTERSECT",VERTEX,{"derivedFrom":[subQ1,subQ0]});Q6=makeQuery(id+"F11.imprint","IMPRINT",FACE,{"disambiguationData":[TD([[makeQuery(id+"F11.imprint","IMPRINT",EDGE,{"disambiguationData":[TD([[subQ2,-1.0]])],"derivedFrom":subQ1}),-1.0]])]});}
            var Q7;
            {var subQ0=sQuery(id+"F11.wireOp",EDGE,"E21.7.1");var subQ1=sQuery(id+"F11.wireOp",EDGE,"E17.0");var subQ2=makeQuery(id+"F11.imprint","INTERSECT",VERTEX,{"derivedFrom":[subQ1,subQ0]});Q7=makeQuery(id+"F11.imprint","IMPRINT",FACE,{"disambiguationData":[TD([[makeQuery(id+"F11.imprint","IMPRINT",EDGE,{"disambiguationData":[TD([[subQ2,-1.0]])],"derivedFrom":subQ1}),-1.0]])]});}
            var Q8;
            {var subQ0=sQuery(id+"F11.wireOp",EDGE,"E21.8.1");var subQ1=sQuery(id+"F11.wireOp",EDGE,"E17.0");var subQ2=makeQuery(id+"F11.imprint","INTERSECT",VERTEX,{"derivedFrom":[subQ1,subQ0]});Q8=makeQuery(id+"F11.imprint","IMPRINT",FACE,{"disambiguationData":[TD([[makeQuery(id+"F11.imprint","IMPRINT",EDGE,{"disambiguationData":[TD([[subQ2,-1.0]])],"derivedFrom":subQ1}),-1.0]])]});}
            var Q9;
            {var subQ0=sQuery(id+"F11.wireOp",EDGE,"E21.9.1");var subQ1=sQuery(id+"F11.wireOp",EDGE,"E17.0");var subQ2=makeQuery(id+"F11.imprint","INTERSECT",VERTEX,{"derivedFrom":[subQ1,subQ0]});Q9=makeQuery(id+"F11.imprint","IMPRINT",FACE,{"disambiguationData":[TD([[makeQuery(id+"F11.imprint","IMPRINT",EDGE,{"disambiguationData":[TD([[subQ2,-1.0]])],"derivedFrom":subQ1}),-1.0]])]});}
            var Q10;
            {var subQ0=sQuery(id+"F11.wireOp",EDGE,"E21.10.1");var subQ1=sQuery(id+"F11.wireOp",EDGE,"E17.0");var subQ2=makeQuery(id+"F11.imprint","INTERSECT",VERTEX,{"derivedFrom":[subQ1,subQ0]});Q10=makeQuery(id+"F11.imprint","IMPRINT",FACE,{"disambiguationData":[TD([[makeQuery(id+"F11.imprint","IMPRINT",EDGE,{"disambiguationData":[TD([[subQ2,-1.0]])],"derivedFrom":subQ1}),-1.0]])]});}
            var Q11;
            {var subQ0=sQuery(id+"F11.wireOp",EDGE,"E21.11.1");var subQ1=sQuery(id+"F11.wireOp",EDGE,"E17.0");var subQ2=makeQuery(id+"F11.imprint","INTERSECT",VERTEX,{"derivedFrom":[subQ1,subQ0]});Q11=makeQuery(id+"F11.imprint","IMPRINT",FACE,{"disambiguationData":[TD([[makeQuery(id+"F11.imprint","IMPRINT",EDGE,{"disambiguationData":[TD([[subQ2,-1.0]])],"derivedFrom":subQ1}),-1.0]])]});}
            var Q12;
            {var subQ0=sQuery(id+"F11.wireOp",EDGE,"E21.12.1");var subQ1=sQuery(id+"F11.wireOp",EDGE,"E17.0");var subQ2=makeQuery(id+"F11.imprint","INTERSECT",VERTEX,{"derivedFrom":[subQ1,subQ0]});Q12=makeQuery(id+"F11.imprint","IMPRINT",FACE,{"disambiguationData":[TD([[makeQuery(id+"F11.imprint","IMPRINT",EDGE,{"disambiguationData":[TD([[subQ2,-1.0]])],"derivedFrom":subQ1}),-1.0]])]});}
            var Q13;
            {var subQ0=sQuery(id+"F11.wireOp",EDGE,"E21.13.1");var subQ1=sQuery(id+"F11.wireOp",EDGE,"E17.0");var subQ2=makeQuery(id+"F11.imprint","INTERSECT",VERTEX,{"derivedFrom":[subQ1,subQ0]});Q13=makeQuery(id+"F11.imprint","IMPRINT",FACE,{"disambiguationData":[TD([[makeQuery(id+"F11.imprint","IMPRINT",EDGE,{"disambiguationData":[TD([[subQ2,-1.0]])],"derivedFrom":subQ1}),-1.0]])]});}
            var Q14;
            {var subQ0=sQuery(id+"F11.wireOp",EDGE,"E21.14.1");var subQ1=sQuery(id+"F11.wireOp",EDGE,"E17.0");var subQ2=makeQuery(id+"F11.imprint","INTERSECT",VERTEX,{"derivedFrom":[subQ1,subQ0]});Q14=makeQuery(id+"F11.imprint","IMPRINT",FACE,{"disambiguationData":[TD([[makeQuery(id+"F11.imprint","IMPRINT",EDGE,{"disambiguationData":[TD([[subQ2,-1.0]])],"derivedFrom":subQ1}),-1.0]])]});}
            var Q15;
            {var subQ0=sQuery(id+"F11.wireOp",EDGE,"E21.15.1");var subQ1=sQuery(id+"F11.wireOp",EDGE,"E17.0");var subQ2=makeQuery(id+"F11.imprint","INTERSECT",VERTEX,{"derivedFrom":[subQ1,subQ0]});Q15=makeQuery(id+"F11.imprint","IMPRINT",FACE,{"disambiguationData":[TD([[makeQuery(id+"F11.imprint","IMPRINT",EDGE,{"disambiguationData":[TD([[subQ2,-1.0]])],"derivedFrom":subQ1}),-1.0]])]});}
            var Q16;
            {var subQ0=sQuery(id+"F11.wireOp",EDGE,"E21.16.1");var subQ1=sQuery(id+"F11.wireOp",EDGE,"E17.0");var subQ2=makeQuery(id+"F11.imprint","INTERSECT",VERTEX,{"derivedFrom":[subQ1,subQ0]});Q16=makeQuery(id+"F11.imprint","IMPRINT",FACE,{"disambiguationData":[TD([[makeQuery(id+"F11.imprint","IMPRINT",EDGE,{"disambiguationData":[TD([[subQ2,-1.0]])],"derivedFrom":subQ1}),-1.0]])]});}
            var Q17;
            {var subQ0=sQuery(id+"F11.wireOp",EDGE,"E21.17.1");var subQ1=sQuery(id+"F11.wireOp",EDGE,"E17.0");var subQ2=makeQuery(id+"F11.imprint","INTERSECT",VERTEX,{"derivedFrom":[subQ1,subQ0]});Q17=makeQuery(id+"F11.imprint","IMPRINT",FACE,{"disambiguationData":[TD([[makeQuery(id+"F11.imprint","IMPRINT",EDGE,{"disambiguationData":[TD([[subQ2,-1.0]])],"derivedFrom":subQ1}),-1.0]])]});}
            extrude(context, id + "F12", {"entities" : qUnion([Q0, Q1, Q2, Q3, Q4, Q5, Q6, Q7, Q8, Q9, Q10, Q11, Q12, Q13, Q14, Q15, Q16, Q17]), "operationType" : NewBodyOperationType.REMOVE, "oppositeDirection" : true, "depth" : 1 * mm});
        }
        {
            var Q0;
            Q0=makeQuery(id+"F4.imprint","IMPRINT",FACE,{"disambiguationData":[TD([[makeQuery(id+"F4.imprint","IMPRINT",EDGE,{"derivedFrom":sQuery(id+"F4.wireOp",EDGE,"E13.0")}),1.0]])]});
            var sketch = newSketch(context, id + "F13", { "sketchPlane" : qUnion([Q0])});
            skText(sketch, "E38", { "text": "START", "fontName": "OpenSans-Bold.ttf"});
            skLineSegment(sketch, "E39", {"start": v(0, 0) * mm, "end": v(47.1, 17.14) * mm, "construction": true});
            skText(sketch, "E40", { "text": "END", "fontName": "OpenSans-Bold.ttf"});
            skLineSegment(sketch, "E41", {"start": v(0, 0) * mm, "end": v(45.98, -16.6) * mm, "construction": true});
            const initialGuessF13  = {"E38": [0.03634, -0.0013, 1, 0, 0.00241], "E40": [0.03685, -0.01466, 0.9397, -0.34202, 0.00241]};
            skSetInitialGuess(sketch, initialGuessF13);
            skSolve(sketch);
        }
        {
            var Q0;
            Q0 = qSketchRegion(id + "F13", true);
            extrude(context, id + "F14", {"entities" : qUnion([Q0]), "operationType" : NewBodyOperationType.REMOVE, "oppositeDirection" : true, "depth" : 0.7 * mm});
        }
        {
            var Q0;
            Q0=makeQuery(id+"F4.imprint","IMPRINT",FACE,{"disambiguationData":[TD([[makeQuery(id+"F4.imprint","IMPRINT",EDGE,{"derivedFrom":sQuery(id+"F4.wireOp",EDGE,"E11")}),1.0]])]});
            var sketch = newSketch(context, id + "F15", { "sketchPlane" : qUnion([Q0])});
            skCircle(sketch, "E42", {"center": v(0, 0) * mm, "radius": 1.5 * mm});
            skSolve(sketch);
        }
        {
            var Q0;
            Q0=makeQuery(id+"F15.imprint","IMPRINT",FACE,{"disambiguationData":[TD([[makeQuery(id+"F15.imprint","IMPRINT",EDGE,{"derivedFrom":sQuery(id+"F15.wireOp",EDGE,"E42")}),1.0]])]});
            extrude(context, id + "F16", {"entities" : qUnion([Q0]), "operationType" : NewBodyOperationType.REMOVE, "oppositeDirection" : true, "depth" : 25 * mm});
        }
    });
